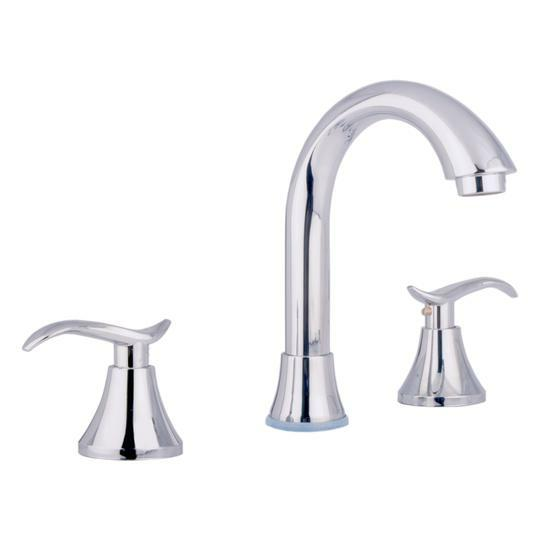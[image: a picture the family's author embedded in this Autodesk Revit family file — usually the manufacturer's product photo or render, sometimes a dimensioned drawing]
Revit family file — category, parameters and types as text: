
# Revit family: 01-1803-11 MEZCLADOR LAVAMANOS PLASTICO 8” TEDESCA
name_source: partatom
category: Plumbing Fixtures
revit_build: Autodesk Revit 2018 (Build: 20170223_1515(x64)
units: mm (PartAtom-declared; Revit-internal decimal feet)

## family parameters
Cut with Voids When Loaded = No
Host = Face
OmniClass Number = 23.31.11.00
Part Type = Normal
Room Calculation Point = No
Round Connector Dimension = Use Diameter
Shared = No

## types (1)
- 01-1803-11
    Alto = 257 mm  [stored 0.843176 ft]
    Alto Aireador = 215 mm
    Ancho = 81.85 mm
    CW Connection = Yes
    Default Elevation = 0 mm  [stored 0 ft]
    Description = Bimando baño
    Eje - Rosca = 203.2 mm  [stored 0.666667 ft]
    Eje- Eje = 187 mm  [stored 0.613517 ft]
    HW Connection = Yes
    Link ficha tecnica = http://infotecnica.gricol.com
    Manija = 80 mm  [stored 0.262467 ft]
    Manufacturer = Gricol
    Model = 01-1803-11
    Plastico ABS Cromado = Plastico - ABS Cromado
    Product Name = MEZCLADOR LAVAMANOS PLASTICO 8” TEDESCA
    Type Image = MEZCLADOR LAVAMANOS PLASTICO 8” TEDESCA.jpg
    URL = https://www.gricol.com
    Vent Connection = No
    Waste Connection = No

note: [stored X ft] marks values corroborated as IEEE doubles in the binary element streams (Revit-internal decimal feet)

## geometry (parser evidence)
native form markers: Blend x4, Sweep x4
no freeform markers — native parametric forms only
